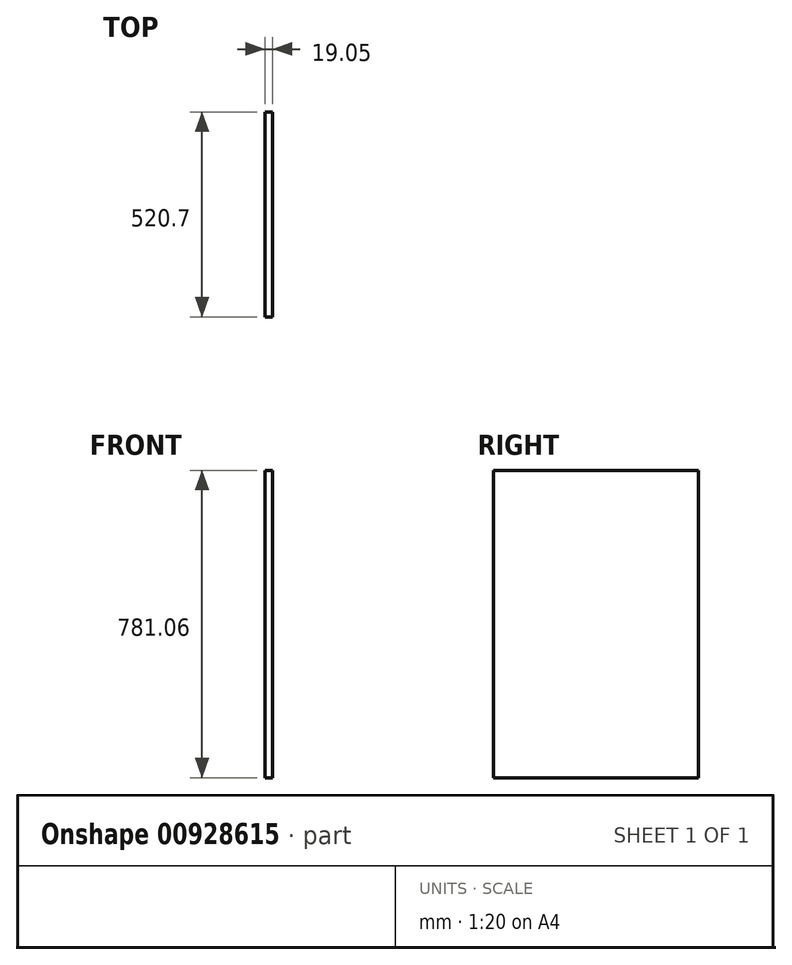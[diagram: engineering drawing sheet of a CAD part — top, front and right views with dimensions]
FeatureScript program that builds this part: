
annotation { "Feature Type Name" : "Feature", "Feature Type Description" : "" }
export const myFeature = defineFeature(function(context is Context, id is Id, definition is map)
    precondition{}
    {
        {
            var Q0;
            Q0=qCreatedBy(makeId("Right.planeOp"),FACE);
            var sketch = newSketch(context, id + "F0", { "sketchPlane" : qUnion([Q0])});
            skLineSegment(sketch, "E0.bottom", {"start": v(260.35, 390.53) * mm, "end": v(-260.35, 390.53) * mm});
            skLineSegment(sketch, "E0.top", {"start": v(260.35, -390.53) * mm, "end": v(-260.35, -390.53) * mm});
            skLineSegment(sketch, "E0.left", {"start": v(260.35, 390.53) * mm, "end": v(260.35, -390.53) * mm});
            skLineSegment(sketch, "E0.right", {"start": v(-260.35, 390.53) * mm, "end": v(-260.35, -390.53) * mm});
            skPoint(sketch, "E0.middle", {"position": v(0, 0) * mm});
            skSolve(sketch);
        }
        {
            var Q0;
            Q0=makeQuery(id+"F0.imprint","IMPRINT",FACE,{"disambiguationData":[TD([[makeQuery(id+"F0.imprint","IMPRINT",EDGE,{"derivedFrom":sQuery(id+"F0.wireOp",EDGE,"E0.bottom")}),1.0]])]});
            extrude(context, id + "F1", {"entities" : qUnion([Q0]), "depth" : 19.05 * mm, "offsetDistance" : 25.4 * mm});
        }
    });
